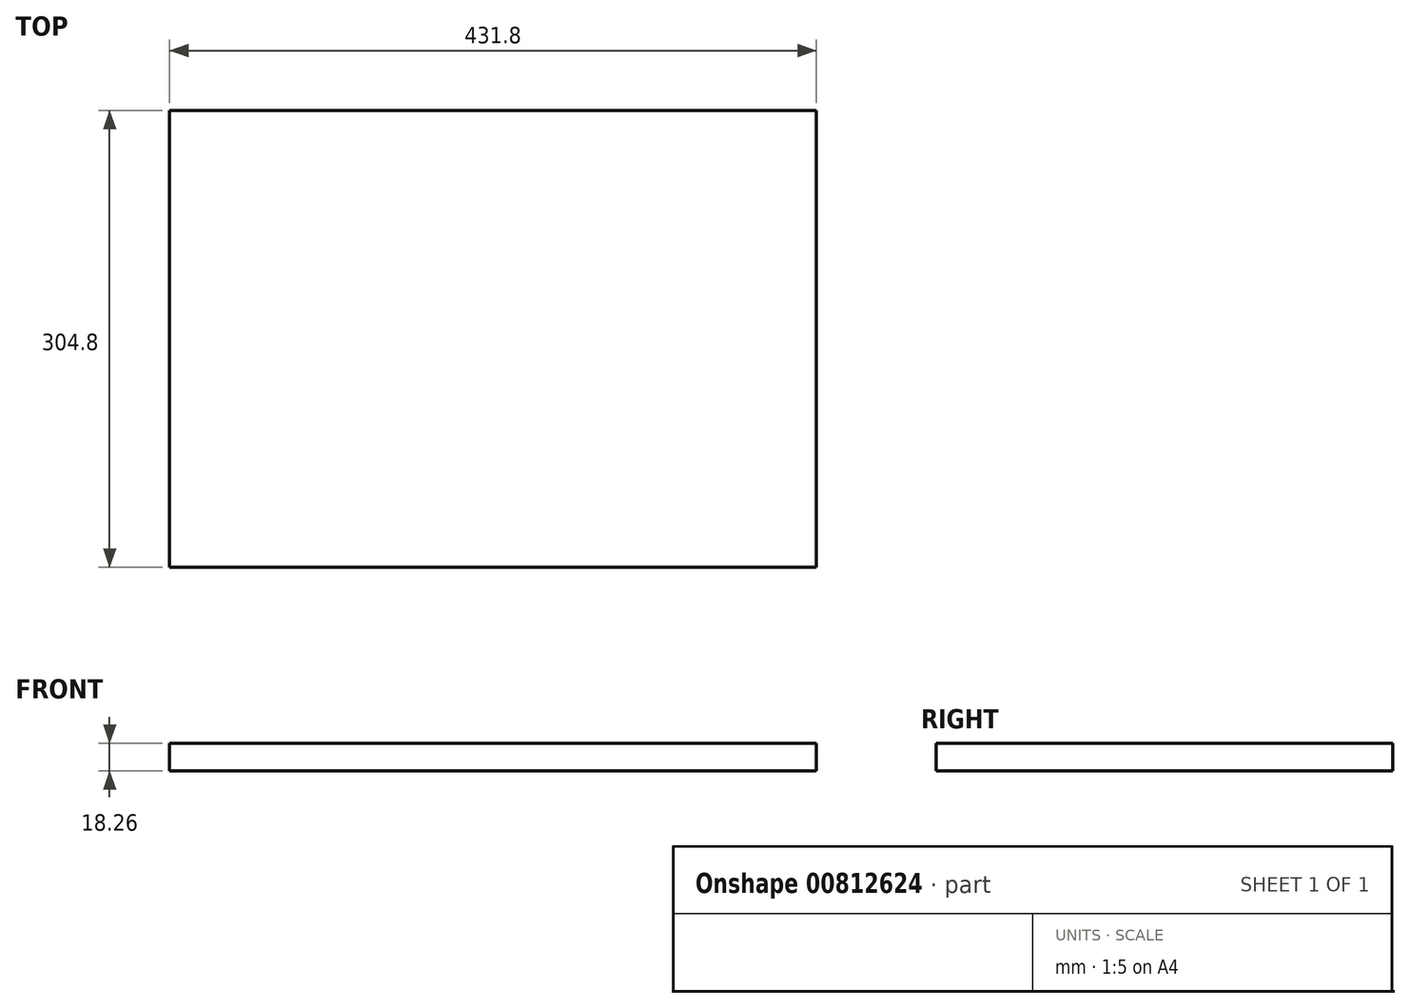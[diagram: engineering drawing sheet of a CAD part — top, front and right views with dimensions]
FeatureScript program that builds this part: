
annotation { "Feature Type Name" : "Feature", "Feature Type Description" : "" }
export const myFeature = defineFeature(function(context is Context, id is Id, definition is map)
    precondition{}
    {
        {
            var Q0;
            Q0=qCreatedBy(makeId("Top.planeOp"),FACE);
            var sketch = newSketch(context, id + "F0", { "sketchPlane" : qUnion([Q0])});
            skLineSegment(sketch, "E0.bottom", {"start": v(215.9, 152.4) * mm, "end": v(-215.9, 152.4) * mm});
            skLineSegment(sketch, "E0.top", {"start": v(215.9, -152.4) * mm, "end": v(-215.9, -152.4) * mm});
            skLineSegment(sketch, "E0.left", {"start": v(215.9, 152.4) * mm, "end": v(215.9, -152.4) * mm});
            skLineSegment(sketch, "E0.right", {"start": v(-215.9, 152.4) * mm, "end": v(-215.9, -152.4) * mm});
            skPoint(sketch, "E0.middle", {"position": v(0, 0) * mm});
            skSolve(sketch);
        }
        {
            var Q0;
            Q0=makeQuery(id+"F0.imprint","IMPRINT",FACE,{"disambiguationData":[TD([[makeQuery(id+"F0.imprint","IMPRINT",EDGE,{"derivedFrom":sQuery(id+"F0.wireOp",EDGE,"E0.bottom")}),1.0]])]});
            extrude(context, id + "F1", {"entities" : qUnion([Q0]), "depth" : 18.26 * mm, "offsetDistance" : 25.4 * mm});
        }
    });
